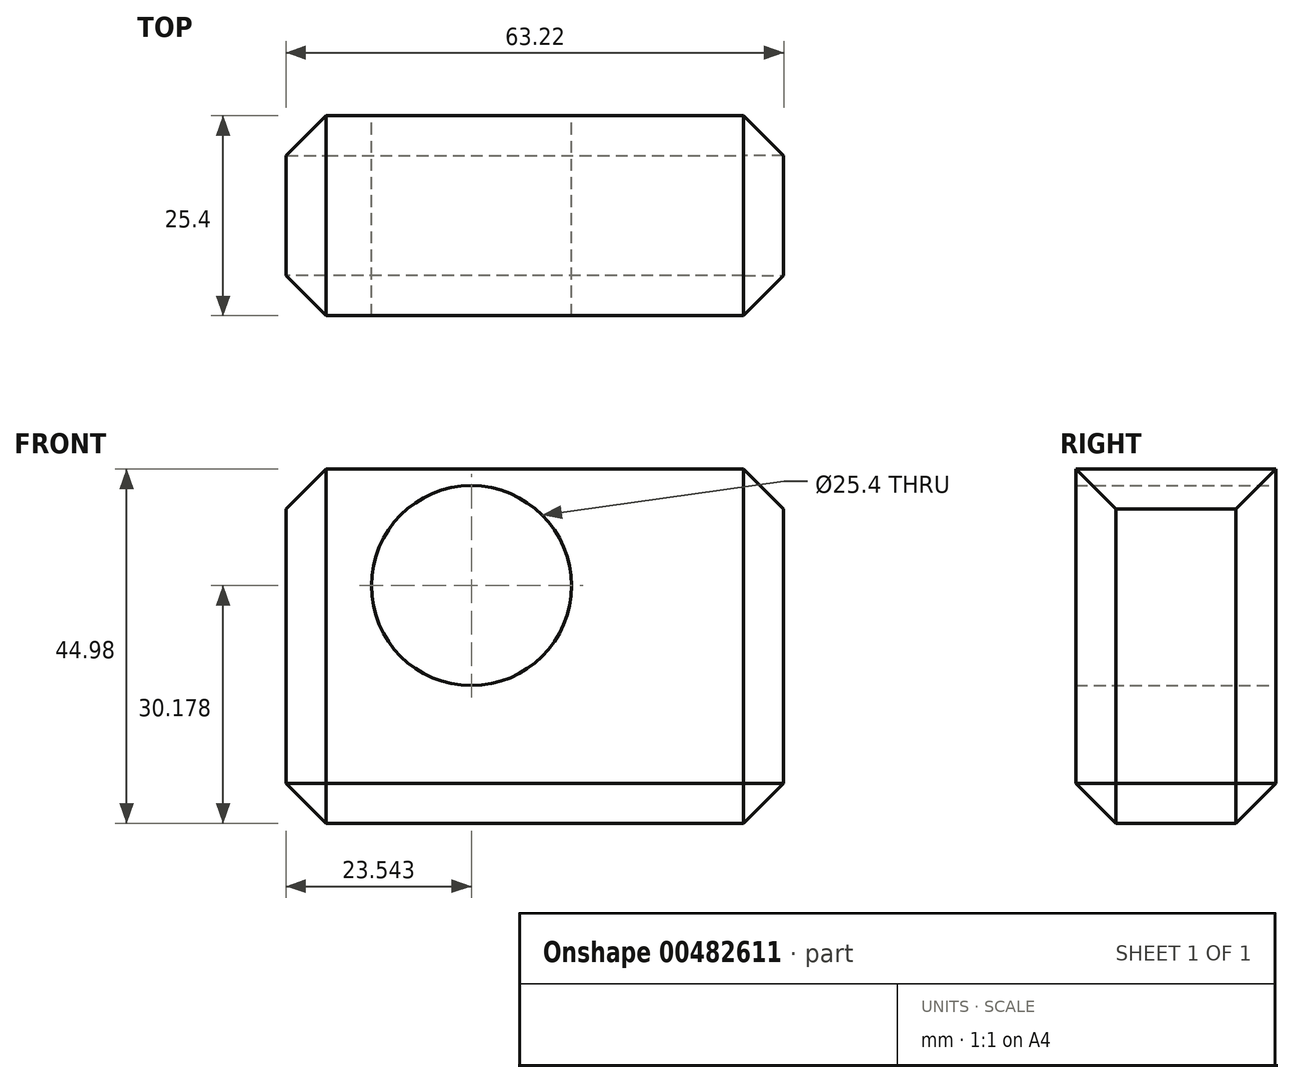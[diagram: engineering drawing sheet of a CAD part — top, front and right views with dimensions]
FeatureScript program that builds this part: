
annotation { "Feature Type Name" : "Feature", "Feature Type Description" : "" }
export const myFeature = defineFeature(function(context is Context, id is Id, definition is map)
    precondition{}
    {
        {
            var Q0;
            Q0=qCreatedBy(makeId("Front.planeOp"),FACE);
            var sketch = newSketch(context, id + "F0", { "sketchPlane" : qUnion([Q0])});
            skLineSegment(sketch, "E0.bottom", {"start": v(-31.6, 22.5) * mm, "end": v(31.6, 22.5) * mm});
            skLineSegment(sketch, "E0.top", {"start": v(-31.6, -22.5) * mm, "end": v(31.6, -22.5) * mm});
            skLineSegment(sketch, "E0.left", {"start": v(-31.6, 22.5) * mm, "end": v(-31.6, -22.5) * mm});
            skLineSegment(sketch, "E0.right", {"start": v(31.6, 22.5) * mm, "end": v(31.6, -22.5) * mm});
            skPoint(sketch, "E0.middle", {"position": v(0, 0) * mm});
            skPoint(sketch, "E1", {"position": v(-24.01, 16.04) * mm});
            skPoint(sketch, "E2", {"position": v(-22.11, -15.66) * mm});
            skPoint(sketch, "E3", {"position": v(25.72, -17.37) * mm});
            skPoint(sketch, "E4", {"position": v(24.96, 16.04) * mm});
            skSolve(sketch);
        }
        {
            var Q0;
            Q0 = qSketchRegion(id + "F0", true);
            extrude(context, id + "F1", {"entities" : qUnion([Q0]), "depth" : 25.4 * mm});
        }
        {
            var Q0;
            Q0=qCreatedBy(makeId("Front.planeOp"),FACE);
            var sketch = newSketch(context, id + "F2", { "sketchPlane" : qUnion([Q0])});
            skPoint(sketch, "E5", {"position": v(-8.07, 7.69) * mm});
            skSolve(sketch);
        }
        {
            var Q0;
            Q0=sQuery(id+"F2.wireOp",VERTEX,"E5");
            var Q1;
            Q1=makeQuery(id+"F1.opExtrude","SWEPT_BODY",BODY,{"disambiguationData":[OSD([sQuery(id+"F0.wireOp",EDGE,"E0.bottom"),sQuery(id+"F0.wireOp",EDGE,"E0.top"),sQuery(id+"F0.wireOp",EDGE,"E0.left"),sQuery(id+"F0.wireOp",EDGE,"E0.right")])]});
            hole(context, id + "F3", {"style" : HoleStyle.SIMPLE, "endStyle" : HoleEndStyle.THROUGH, "oppositeDirection" : true, "holeDiameter" : 25.4 * mm, "isTappedThrough" : true, "tappedDepth" : 12.7 * mm, "tapClearance" : 3, "locations" : qUnion([Q0]), "scope" : qUnion([Q1])});
        }
        {
            var Q0;
            Q0=makeQuery(id+"F1.opExtrude","SWEPT_FACE",FACE,{"disambiguationData":[OSD([sQuery(id+"F0.wireOp",EDGE,"E0.right")])]});
            var Q1;
            Q1=makeQuery(id+"F1.opExtrude","SWEPT_FACE",FACE,{"disambiguationData":[OSD([sQuery(id+"F0.wireOp",EDGE,"E0.left")])]});
            var Q2;
            Q2=makeQuery(id+"F1.opExtrude","SWEPT_FACE",FACE,{"disambiguationData":[OSD([sQuery(id+"F0.wireOp",EDGE,"E0.top")])]});
            chamfer(context, id + "F4", {"entities" : qUnion([Q0, Q1, Q2]), "width" : 5.08 * mm, "tangentPropagation" : true});
        }
    });
